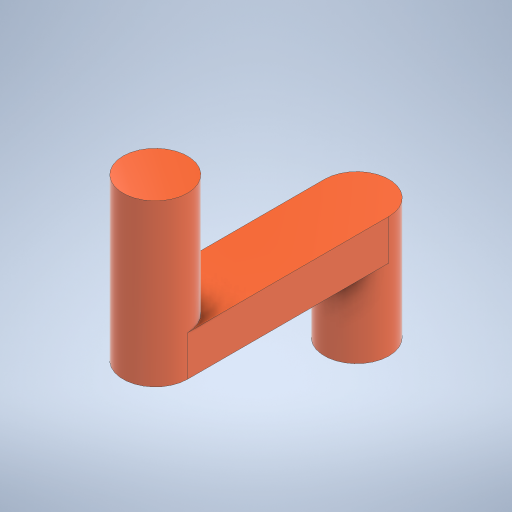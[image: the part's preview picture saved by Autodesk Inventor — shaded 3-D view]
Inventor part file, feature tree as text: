
AUTODESK INVENTOR PART (.ipt)
format: ipt  version: 2024 (Build 280153020, 153B)  size: 240,640 bytes
history: native  units: mm
features: extrude x3, sketch x3
ambient origin geometry x8: Origin, YZ Plane, XZ Plane, XY Plane, X Axis, Y Axis, Z Axis, Center Point
bodies: Solid1 (feature_tree)
feature tree (6):
  extrude  "Extrusion1"  Depth=10.0mm TaperAngle=0.0deg
  extrude  "Extrusion2"  Depth=5.0mm TaperAngle=0.0deg
  extrude  "Extrusion3"  [1 undecoded]
  sketch  "Sketch1"  dims[d0=8.0mm d1=10.0mm d2=0.0mm]
  sketch  "Sketch2"  dims[d3=25.0mm d4=5.0mm d5=0.0mm]
  sketch  "Sketch3"  dims[d6=15.0mm d7=0.0mm]
note: 1 required parameter value undecoded (feature->parameter linkage not recoverable at this tier; creation-order binding heuristic only, values carry confidence <= 0.55)
